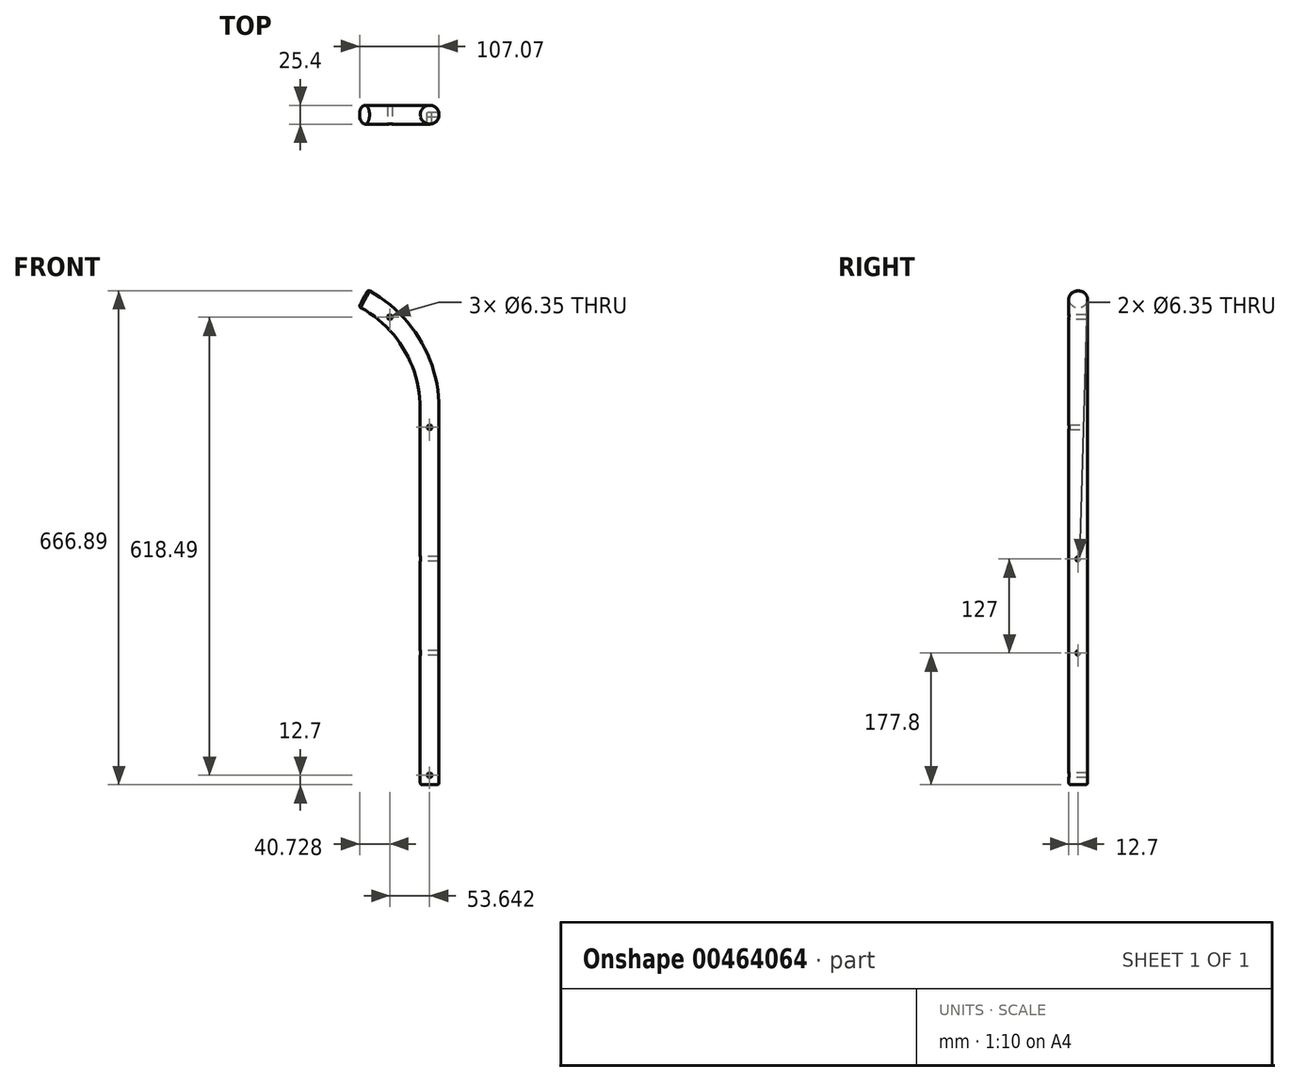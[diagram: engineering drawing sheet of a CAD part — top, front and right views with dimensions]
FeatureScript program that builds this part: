
annotation { "Feature Type Name" : "Feature", "Feature Type Description" : "" }
export const myFeature = defineFeature(function(context is Context, id is Id, definition is map)
    precondition{}
    {
        {
            var Q0;
            Q0=qCreatedBy(makeId("Front.planeOp"),FACE);
            var sketch = newSketch(context, id + "F0", { "sketchPlane" : qUnion([Q0])});
            skLineSegment(sketch, "E0", {"start": v(0, 0) * mm, "end": v(0, 508) * mm});
            skArc(sketch, "E1", {"start": v(0, 508) * mm, "mid": v(-24.04, 594.68) * mm, "end": v(-89.3, 656.6) * mm});
            skLineSegment(sketch, "E2", {"start": v(-89.3, 656.6) * mm, "end": v(-89.3, 508) * mm});
            skLineSegment(sketch, "E3", {"start": v(-89.3, 508) * mm, "end": v(0, 508) * mm});
            skSolve(sketch);
        }
        {
            var Q0;
            Q0=qCreatedBy(makeId("Top.planeOp"),FACE);
            var sketch = newSketch(context, id + "F1", { "sketchPlane" : qUnion([Q0])});
            skCircle(sketch, "E4", {"center": v(0, 0) * mm, "radius": 12.7 * mm});
            skSolve(sketch);
        }
        {
            var Q0;
            Q0=makeQuery(id+"F1.imprint","IMPRINT",FACE,{"disambiguationData":[TD([[makeQuery(id+"F1.imprint","IMPRINT",EDGE,{"derivedFrom":sQuery(id+"F1.wireOp",EDGE,"E4")}),1.0]])]});
            var Q1;
            Q1=sQuery(id+"F0.wireOp",EDGE,"E1");
            var Q2;
            Q2=sQuery(id+"F0.wireOp",EDGE,"E0");
            sweep(context, id + "F2", {"profiles" : qUnion([Q0]), "path" : qUnion([Q1, Q2])});
        }
        {
            var Q0;
            Q0=makeQuery(id+"F2.opSweep","CAP_EDGE",EDGE,{"disambiguationData":[OSD([sQuery(id+"F0.wireOp",VERTEX,"E1.end"),sQuery(id+"F1.wireOp",EDGE,"E4")])],"isStart":false});
            var Q1;
            Q1=makeQuery(id+"F2.opSweep","CAP_EDGE",EDGE,{"disambiguationData":[OSD([sQuery(id+"F0.wireOp",VERTEX,"E0.start"),sQuery(id+"F1.wireOp",EDGE,"E4")])],"isStart":true});
            fillet(context, id + "F3", {"entities" : qUnion([Q0, Q1]), "radius" : 2.54 * mm, "tangentPropagation" : true, "allowEdgeOverflow" : false});
        }
        {
            var Q0;
            Q0=qCreatedBy(makeId("Front.planeOp"),FACE);
            cPlane(context, id + "F4", {"entities" : qUnion([Q0]), "cplaneType" : CPlaneType.OFFSET, "offset" : 12.7 * mm, "width" : 152.4 * mm, "height" : 152.4 * mm});
        }
        {
            var Q0;
            Q0=qCreatedBy(id+"F4.planeOp",FACE);
            var sketch = newSketch(context, id + "F5", { "sketchPlane" : qUnion([Q0])});
            skLineSegment(sketch, "E5", {"start": v(0, 0) * mm, "end": v(0, 482.6) * mm});
            skCircle(sketch, "E6", {"center": v(0, 482.6) * mm, "radius": 3.18 * mm});
            skSolve(sketch);
        }
        {
            var Q0;
            Q0 = qSketchRegion(id + "F5", true);
            extrude(context, id + "F6", {"entities" : qUnion([Q0]), "operationType" : NewBodyOperationType.REMOVE, "depth" : 6.35 * mm, "hasSecondDirection" : true, "secondDirectionOppositeDirection" : true, "secondDirectionDepth" : 31.75 * mm});
        }
        {
            var Q0;
            Q0=qCreatedBy(id+"F4.planeOp",FACE);
            var sketch = newSketch(context, id + "F7", { "sketchPlane" : qUnion([Q0])});
            skCircle(sketch, "E7", {"center": v(-53.64, 631.2) * mm, "radius": 3.18 * mm});
            skSolve(sketch);
        }
        {
            var Q0;
            Q0 = qSketchRegion(id + "F7", true);
            extrude(context, id + "F8", {"entities" : qUnion([Q0]), "operationType" : NewBodyOperationType.REMOVE, "oppositeDirection" : true, "depth" : 40.64 * mm});
        }
        {
            var Q0;
            Q0=qCreatedBy(makeId("Front.planeOp"),FACE);
            cPlane(context, id + "F9", {"entities" : qUnion([Q0]), "cplaneType" : CPlaneType.OFFSET, "offset" : 12.7 * mm, "oppositeDirection" : true, "width" : 152.4 * mm, "height" : 152.4 * mm});
        }
        {
            var Q0;
            Q0=qCreatedBy(id+"F9.planeOp",FACE);
            var sketch = newSketch(context, id + "F10", { "sketchPlane" : qUnion([Q0])});
            skLineSegment(sketch, "E8", {"start": v(0, 0) * mm, "end": v(0, 508) * mm});
            skLineSegment(sketch, "E9", {"start": v(0, 508) * mm, "end": v(-89.3, 508) * mm});
            skCircle(sketch, "E10", {"center": v(-53.64, 631.2) * mm, "radius": 3.18 * mm});
            skSolve(sketch);
        }
        {
            var Q0;
            Q0 = qSketchRegion(id + "F10", true);
            extrude(context, id + "F11", {"entities" : qUnion([Q0]), "operationType" : NewBodyOperationType.REMOVE, "depth" : 6.35 * mm});
        }
        {
            var Q0;
            Q0=qCreatedBy(makeId("Right.planeOp"),FACE);
            var sketch = newSketch(context, id + "F12", { "sketchPlane" : qUnion([Q0])});
            skCircle(sketch, "E11", {"center": v(0, 304.8) * mm, "radius": 3.18 * mm});
            skCircle(sketch, "E12", {"center": v(0, 177.8) * mm, "radius": 3.18 * mm});
            skSolve(sketch);
        }
        {
            var Q0;
            Q0 = qSketchRegion(id + "F12", true);
            extrude(context, id + "F13", {"entities" : qUnion([Q0]), "operationType" : NewBodyOperationType.REMOVE, "depth" : 19.05 * mm, "hasSecondDirection" : true, "secondDirectionOppositeDirection" : true, "secondDirectionDepth" : 25.4 * mm});
        }
        {
            var Q0;
            Q0=qCreatedBy(makeId("Front.planeOp"),FACE);
            var sketch = newSketch(context, id + "F14", { "sketchPlane" : qUnion([Q0])});
            skLineSegment(sketch, "E13", {"start": v(0, 0) * mm, "end": v(0, 12.7) * mm});
            skCircle(sketch, "E14", {"center": v(0, 12.7) * mm, "radius": 3.18 * mm});
            skSolve(sketch);
        }
        {
            var Q0;
            Q0 = qSketchRegion(id + "F14", true);
            extrude(context, id + "F15", {"entities" : qUnion([Q0]), "operationType" : NewBodyOperationType.REMOVE, "oppositeDirection" : true, "depth" : 25.4 * mm, "hasSecondDirection" : true, "secondDirectionOppositeDirection" : false, "secondDirectionDepth" : 25.4 * mm});
        }
    });
